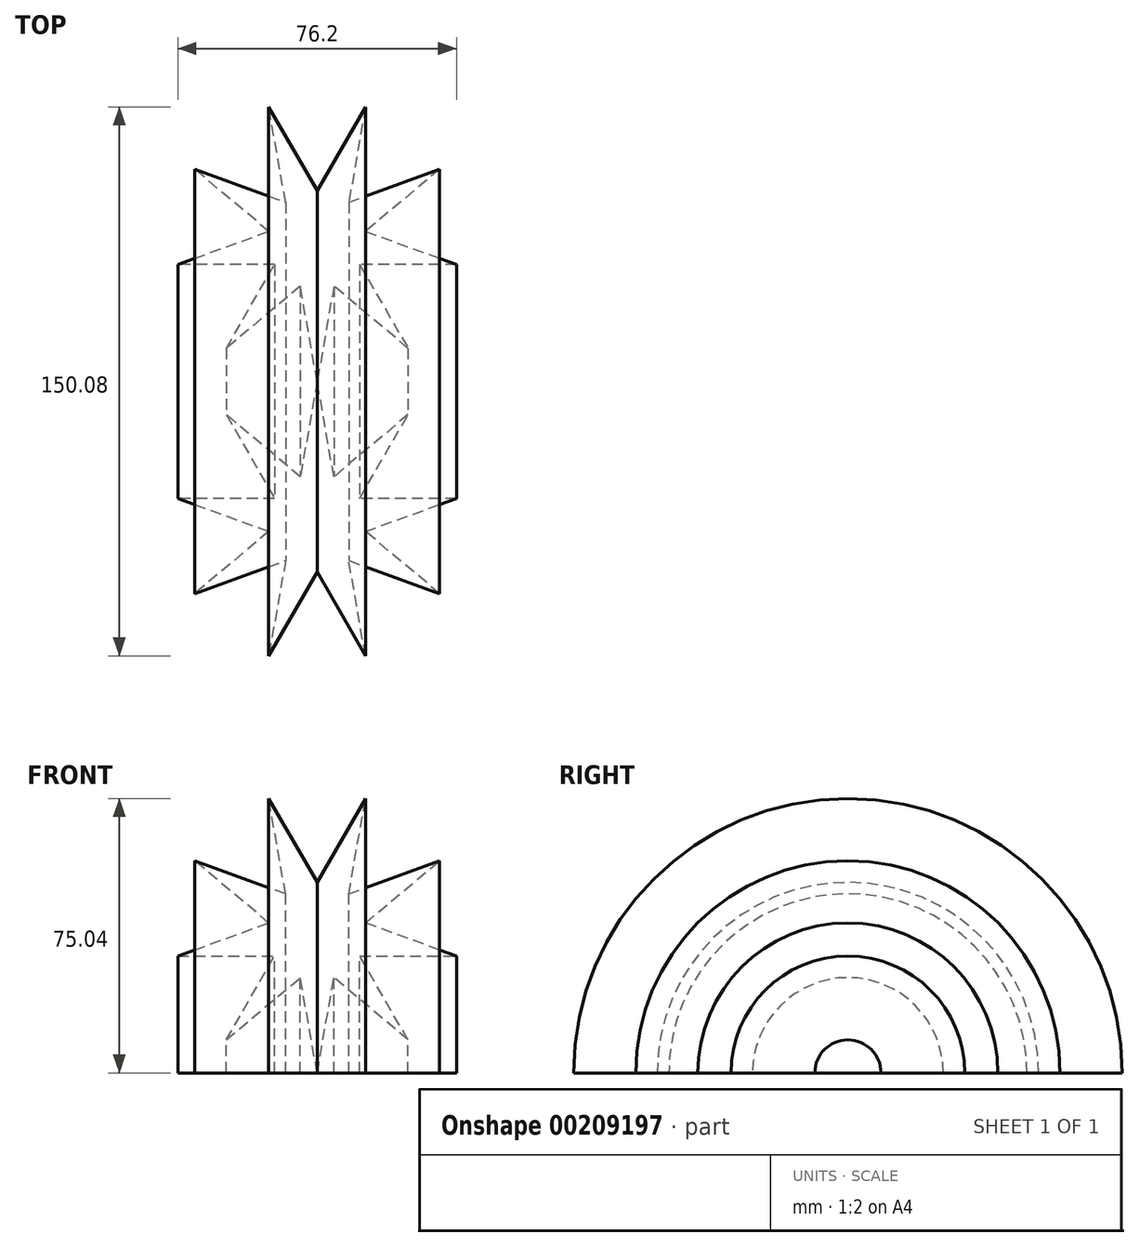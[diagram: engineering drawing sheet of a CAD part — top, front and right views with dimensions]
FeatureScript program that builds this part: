
annotation { "Feature Type Name" : "Feature", "Feature Type Description" : "" }
export const myFeature = defineFeature(function(context is Context, id is Id, definition is map)
    precondition{}
    {
        {
            var Q0;
            Q0=qCreatedBy(makeId("Top.planeOp"),FACE);
            var sketch = newSketch(context, id + "F0", { "sketchPlane" : qUnion([Q0])});
            skLineSegment(sketch, "E0", {"start": v(0, 0) * mm, "end": v(-13.23, -75.04) * mm});
            skLineSegment(sketch, "E1", {"start": v(-13.23, -75.04) * mm, "end": v(24.87, -9.05) * mm});
            skLineSegment(sketch, "E2", {"start": v(24.87, -9.05) * mm, "end": v(-33.5, -58.03) * mm});
            skLineSegment(sketch, "E3", {"start": v(-33.5, -58.03) * mm, "end": v(38.1, -31.97) * mm});
            skLineSegment(sketch, "E4", {"start": v(38.1, -31.97) * mm, "end": v(-38.1, -31.97) * mm});
            skLineSegment(sketch, "E5", {"start": v(-38.1, -31.97) * mm, "end": v(33.5, -58.03) * mm});
            skLineSegment(sketch, "E6", {"start": v(33.5, -58.03) * mm, "end": v(-24.87, -9.05) * mm});
            skLineSegment(sketch, "E7", {"start": v(-24.87, -9.05) * mm, "end": v(13.23, -75.04) * mm});
            skLineSegment(sketch, "E8", {"start": v(13.23, -75.04) * mm, "end": v(0, 0) * mm});
            skSolve(sketch);
        }
        {
            var Q0;
            Q0=qCreatedBy(makeId("Top.planeOp"),FACE);
            var sketch = newSketch(context, id + "F1", { "sketchPlane" : qUnion([Q0])});
            skLineSegment(sketch, "E9", {"start": v(31.65, 0) * mm, "end": v(-31.65, 0) * mm});
            skSolve(sketch);
        }
        {
            var Q0;
            {var subQ0=sQuery(id+"F0.wireOp",EDGE,"E8");var subQ1=sQuery(id+"F0.wireOp",EDGE,"E1");var subQ2=makeQuery(id+"F0.imprint","INTERSECT",VERTEX,{"derivedFrom":[subQ1,subQ0]});Q0=makeQuery(id+"F0.imprint","IMPRINT",FACE,{"disambiguationData":[TD([[makeQuery(id+"F0.imprint","IMPRINT",EDGE,{"disambiguationData":[TD([[subQ2,-1.0]])],"derivedFrom":subQ1}),1.0]])]});}
            var Q1;
            {var subQ0=sQuery(id+"F0.wireOp",EDGE,"E4");var subQ1=sQuery(id+"F0.wireOp",EDGE,"E1");var subQ2=makeQuery(id+"F0.imprint","INTERSECT",VERTEX,{"derivedFrom":[subQ1,subQ0]});Q1=makeQuery(id+"F0.imprint","IMPRINT",FACE,{"disambiguationData":[TD([[makeQuery(id+"F0.imprint","IMPRINT",EDGE,{"disambiguationData":[TD([[subQ2,1.0]])],"derivedFrom":subQ1}),-1.0]])]});}
            var Q2;
            {var subQ0=sQuery(id+"F0.wireOp",EDGE,"E3");var subQ1=sQuery(id+"F0.wireOp",EDGE,"E0");var subQ2=makeQuery(id+"F0.imprint","INTERSECT",VERTEX,{"derivedFrom":[subQ1,subQ0]});Q2=makeQuery(id+"F0.imprint","IMPRINT",FACE,{"disambiguationData":[TD([[makeQuery(id+"F0.imprint","IMPRINT",EDGE,{"disambiguationData":[TD([[subQ2,1.0]])],"derivedFrom":subQ1}),1.0]])]});}
            var Q3;
            {var subQ0=sQuery(id+"F0.wireOp",EDGE,"E8");var subQ1=sQuery(id+"F0.wireOp",EDGE,"E1");var subQ2=makeQuery(id+"F0.imprint","INTERSECT",VERTEX,{"derivedFrom":[subQ1,subQ0]});Q3=makeQuery(id+"F0.imprint","IMPRINT",FACE,{"disambiguationData":[TD([[makeQuery(id+"F0.imprint","IMPRINT",EDGE,{"disambiguationData":[TD([[subQ2,-1.0]])],"derivedFrom":subQ1}),-1.0]])]});}
            var Q4;
            {var subQ0=sQuery(id+"F0.wireOp",EDGE,"E3");var subQ1=sQuery(id+"F0.wireOp",EDGE,"E0");var subQ2=makeQuery(id+"F0.imprint","INTERSECT",VERTEX,{"derivedFrom":[subQ1,subQ0]});Q4=makeQuery(id+"F0.imprint","IMPRINT",FACE,{"disambiguationData":[TD([[makeQuery(id+"F0.imprint","IMPRINT",EDGE,{"disambiguationData":[TD([[subQ2,1.0]])],"derivedFrom":subQ1}),-1.0]])]});}
            var Q5;
            {var subQ0=sQuery(id+"F0.wireOp",EDGE,"E8");var subQ1=sQuery(id+"F0.wireOp",EDGE,"E2");var subQ2=makeQuery(id+"F0.imprint","INTERSECT",VERTEX,{"derivedFrom":[subQ1,subQ0]});Q5=makeQuery(id+"F0.imprint","IMPRINT",FACE,{"disambiguationData":[TD([[makeQuery(id+"F0.imprint","IMPRINT",EDGE,{"disambiguationData":[TD([[subQ2,-1.0]])],"derivedFrom":subQ1}),1.0]])]});}
            var Q6;
            {var subQ0=sQuery(id+"F0.wireOp",EDGE,"E5");var subQ1=sQuery(id+"F0.wireOp",EDGE,"E2");var subQ2=makeQuery(id+"F0.imprint","INTERSECT",VERTEX,{"derivedFrom":[subQ1,subQ0]});Q6=makeQuery(id+"F0.imprint","IMPRINT",FACE,{"disambiguationData":[TD([[makeQuery(id+"F0.imprint","IMPRINT",EDGE,{"disambiguationData":[TD([[subQ2,1.0]])],"derivedFrom":subQ1}),-1.0]])]});}
            var Q7;
            {var subQ0=sQuery(id+"F0.wireOp",EDGE,"E6");var subQ1=sQuery(id+"F0.wireOp",EDGE,"E3");var subQ2=makeQuery(id+"F0.imprint","INTERSECT",VERTEX,{"derivedFrom":[subQ1,subQ0]});Q7=makeQuery(id+"F0.imprint","IMPRINT",FACE,{"disambiguationData":[TD([[makeQuery(id+"F0.imprint","IMPRINT",EDGE,{"disambiguationData":[TD([[subQ2,1.0]])],"derivedFrom":subQ1}),-1.0]])]});}
            var Q8;
            {var subQ0=sQuery(id+"F0.wireOp",EDGE,"E7");var subQ1=sQuery(id+"F0.wireOp",EDGE,"E1");var subQ2=makeQuery(id+"F0.imprint","INTERSECT",VERTEX,{"derivedFrom":[subQ1,subQ0]});Q8=makeQuery(id+"F0.imprint","IMPRINT",FACE,{"disambiguationData":[TD([[makeQuery(id+"F0.imprint","IMPRINT",EDGE,{"disambiguationData":[TD([[subQ2,-1.0]])],"derivedFrom":subQ1}),1.0]])]});}
            var Q9;
            {var subQ0=sQuery(id+"F0.wireOp",EDGE,"E2");var subQ1=sQuery(id+"F0.wireOp",EDGE,"E0");var subQ2=makeQuery(id+"F0.imprint","INTERSECT",VERTEX,{"derivedFrom":[subQ1,subQ0]});Q9=makeQuery(id+"F0.imprint","IMPRINT",FACE,{"disambiguationData":[TD([[makeQuery(id+"F0.imprint","IMPRINT",EDGE,{"disambiguationData":[TD([[subQ2,-1.0]])],"derivedFrom":subQ1}),-1.0]])]});}
            var Q10;
            {var subQ5=sQuery(id+"F0.wireOp",EDGE,"E2");var subQ6=sQuery(id+"F0.wireOp",EDGE,"E0");var subQ7=makeQuery(id+"F0.imprint","INTERSECT",VERTEX,{"derivedFrom":[subQ6,subQ5]});Q10=makeQuery(id+"F0.imprint","IMPRINT",FACE,{"disambiguationData":[TD([[makeQuery(id+"F0.imprint","IMPRINT",EDGE,{"disambiguationData":[TD([[subQ7,-1.0]])],"derivedFrom":subQ6}),1.0]])]});}
            var Q11;
            {var subQ0=sQuery(id+"F0.wireOp",EDGE,"E5");var subQ1=sQuery(id+"F0.wireOp",EDGE,"E1");var subQ2=makeQuery(id+"F0.imprint","INTERSECT",VERTEX,{"derivedFrom":[subQ1,subQ0]});Q11=makeQuery(id+"F0.imprint","IMPRINT",FACE,{"disambiguationData":[TD([[makeQuery(id+"F0.imprint","IMPRINT",EDGE,{"disambiguationData":[TD([[subQ2,-1.0]])],"derivedFrom":subQ1}),-1.0]])]});}
            var Q12;
            {var subQ0=sQuery(id+"F0.wireOp",EDGE,"E6");var subQ1=sQuery(id+"F0.wireOp",EDGE,"E0");var subQ2=makeQuery(id+"F0.imprint","INTERSECT",VERTEX,{"derivedFrom":[subQ1,subQ0]});Q12=makeQuery(id+"F0.imprint","IMPRINT",FACE,{"disambiguationData":[TD([[makeQuery(id+"F0.imprint","IMPRINT",EDGE,{"disambiguationData":[TD([[subQ2,-1.0]])],"derivedFrom":subQ1}),-1.0]])]});}
            var Q13;
            {var subQ0=sQuery(id+"F0.wireOp",EDGE,"E1");var subQ1=sQuery(id+"F0.wireOp",EDGE,"E0");var subQ2=makeQuery(id+"F0.imprint","INTERSECT",VERTEX,{"derivedFrom":[subQ1,subQ0]});Q13=makeQuery(id+"F0.imprint","IMPRINT",FACE,{"disambiguationData":[TD([[makeQuery(id+"F0.imprint","IMPRINT",EDGE,{"disambiguationData":[TD([[subQ2,1.0]])],"derivedFrom":subQ1}),1.0]])]});}
            var Q14;
            {var subQ0=sQuery(id+"F0.wireOp",EDGE,"E4");var subQ1=sQuery(id+"F0.wireOp",EDGE,"E1");var subQ2=makeQuery(id+"F0.imprint","INTERSECT",VERTEX,{"derivedFrom":[subQ1,subQ0]});Q14=makeQuery(id+"F0.imprint","IMPRINT",FACE,{"disambiguationData":[TD([[makeQuery(id+"F0.imprint","IMPRINT",EDGE,{"disambiguationData":[TD([[subQ2,1.0]])],"derivedFrom":subQ1}),1.0]])]});}
            var Q15;
            {var subQ0=sQuery(id+"F0.wireOp",EDGE,"E7");var subQ1=sQuery(id+"F0.wireOp",EDGE,"E1");var subQ2=makeQuery(id+"F0.imprint","INTERSECT",VERTEX,{"derivedFrom":[subQ1,subQ0]});Q15=makeQuery(id+"F0.imprint","IMPRINT",FACE,{"disambiguationData":[TD([[makeQuery(id+"F0.imprint","IMPRINT",EDGE,{"disambiguationData":[TD([[subQ2,-1.0]])],"derivedFrom":subQ1}),-1.0]])]});}
            var Q16;
            {var subQ0=sQuery(id+"F0.wireOp",EDGE,"E2");var subQ1=sQuery(id+"F0.wireOp",EDGE,"E1");var subQ2=makeQuery(id+"F0.imprint","INTERSECT",VERTEX,{"derivedFrom":[subQ1,subQ0]});Q16=makeQuery(id+"F0.imprint","IMPRINT",FACE,{"disambiguationData":[TD([[makeQuery(id+"F0.imprint","IMPRINT",EDGE,{"disambiguationData":[TD([[subQ2,1.0]])],"derivedFrom":subQ1}),1.0]])]});}
            var Q17;
            {var subQ0=sQuery(id+"F0.wireOp",EDGE,"E7");var subQ1=sQuery(id+"F0.wireOp",EDGE,"E0");var subQ2=makeQuery(id+"F0.imprint","INTERSECT",VERTEX,{"derivedFrom":[subQ1,subQ0]});Q17=makeQuery(id+"F0.imprint","IMPRINT",FACE,{"disambiguationData":[TD([[makeQuery(id+"F0.imprint","IMPRINT",EDGE,{"disambiguationData":[TD([[subQ2,-1.0]])],"derivedFrom":subQ1}),-1.0]])]});}
            var Q18;
            {var subQ0=sQuery(id+"F0.wireOp",EDGE,"E6");var subQ1=sQuery(id+"F0.wireOp",EDGE,"E0");var subQ2=makeQuery(id+"F0.imprint","INTERSECT",VERTEX,{"derivedFrom":[subQ1,subQ0]});Q18=makeQuery(id+"F0.imprint","IMPRINT",FACE,{"disambiguationData":[TD([[makeQuery(id+"F0.imprint","IMPRINT",EDGE,{"disambiguationData":[TD([[subQ2,-1.0]])],"derivedFrom":subQ1}),1.0]])]});}
            var Q19;
            {var subQ0=sQuery(id+"F0.wireOp",EDGE,"E4");var subQ1=sQuery(id+"F0.wireOp",EDGE,"E0");var subQ2=makeQuery(id+"F0.imprint","INTERSECT",VERTEX,{"derivedFrom":[subQ1,subQ0]});Q19=makeQuery(id+"F0.imprint","IMPRINT",FACE,{"disambiguationData":[TD([[makeQuery(id+"F0.imprint","IMPRINT",EDGE,{"disambiguationData":[TD([[subQ2,-1.0]])],"derivedFrom":subQ1}),-1.0]])]});}
            var Q20;
            {var subQ0=sQuery(id+"F0.wireOp",EDGE,"E7");var subQ1=sQuery(id+"F0.wireOp",EDGE,"E3");var subQ2=makeQuery(id+"F0.imprint","INTERSECT",VERTEX,{"derivedFrom":[subQ1,subQ0]});Q20=makeQuery(id+"F0.imprint","IMPRINT",FACE,{"disambiguationData":[TD([[makeQuery(id+"F0.imprint","IMPRINT",EDGE,{"disambiguationData":[TD([[subQ2,-1.0]])],"derivedFrom":subQ1}),1.0]])]});}
            var Q21;
            {var subQ0=sQuery(id+"F0.wireOp",EDGE,"E6");var subQ1=sQuery(id+"F0.wireOp",EDGE,"E2");var subQ2=makeQuery(id+"F0.imprint","INTERSECT",VERTEX,{"derivedFrom":[subQ1,subQ0]});Q21=makeQuery(id+"F0.imprint","IMPRINT",FACE,{"disambiguationData":[TD([[makeQuery(id+"F0.imprint","IMPRINT",EDGE,{"disambiguationData":[TD([[subQ2,-1.0]])],"derivedFrom":subQ1}),1.0]])]});}
            var Q22;
            {var subQ0=sQuery(id+"F0.wireOp",EDGE,"E7");var subQ1=sQuery(id+"F0.wireOp",EDGE,"E0");var subQ2=makeQuery(id+"F0.imprint","INTERSECT",VERTEX,{"derivedFrom":[subQ1,subQ0]});Q22=makeQuery(id+"F0.imprint","IMPRINT",FACE,{"disambiguationData":[TD([[makeQuery(id+"F0.imprint","IMPRINT",EDGE,{"disambiguationData":[TD([[subQ2,-1.0]])],"derivedFrom":subQ1}),1.0]])]});}
            var Q23;
            {var subQ0=sQuery(id+"F0.wireOp",EDGE,"E5");var subQ1=sQuery(id+"F0.wireOp",EDGE,"E1");var subQ2=makeQuery(id+"F0.imprint","INTERSECT",VERTEX,{"derivedFrom":[subQ1,subQ0]});Q23=makeQuery(id+"F0.imprint","IMPRINT",FACE,{"disambiguationData":[TD([[makeQuery(id+"F0.imprint","IMPRINT",EDGE,{"disambiguationData":[TD([[subQ2,-1.0]])],"derivedFrom":subQ1}),1.0]])]});}
            var Q24;
            {var subQ0=sQuery(id+"F0.wireOp",EDGE,"E8");var subQ1=sQuery(id+"F0.wireOp",EDGE,"E4");var subQ2=makeQuery(id+"F0.imprint","INTERSECT",VERTEX,{"derivedFrom":[subQ1,subQ0]});Q24=makeQuery(id+"F0.imprint","IMPRINT",FACE,{"disambiguationData":[TD([[makeQuery(id+"F0.imprint","IMPRINT",EDGE,{"disambiguationData":[TD([[subQ2,-1.0]])],"derivedFrom":subQ1}),1.0]])]});}
            var Q25;
            {var subQ0=sQuery(id+"F0.wireOp",EDGE,"E4");var subQ1=sQuery(id+"F0.wireOp",EDGE,"E0");var subQ2=makeQuery(id+"F0.imprint","INTERSECT",VERTEX,{"derivedFrom":[subQ1,subQ0]});Q25=makeQuery(id+"F0.imprint","IMPRINT",FACE,{"disambiguationData":[TD([[makeQuery(id+"F0.imprint","IMPRINT",EDGE,{"disambiguationData":[TD([[subQ2,-1.0]])],"derivedFrom":subQ1}),1.0]])]});}
            var Q26;
            {var subQ0=sQuery(id+"F0.wireOp",EDGE,"E3");var subQ1=sQuery(id+"F0.wireOp",EDGE,"E1");var subQ2=makeQuery(id+"F0.imprint","INTERSECT",VERTEX,{"derivedFrom":[subQ1,subQ0]});Q26=makeQuery(id+"F0.imprint","IMPRINT",FACE,{"disambiguationData":[TD([[makeQuery(id+"F0.imprint","IMPRINT",EDGE,{"disambiguationData":[TD([[subQ2,-1.0]])],"derivedFrom":subQ1}),-1.0]])]});}
            var Q27;
            {var subQ0=sQuery(id+"F0.wireOp",EDGE,"E8");var subQ1=sQuery(id+"F0.wireOp",EDGE,"E0");var subQ2=makeQuery(id+"F0.imprint","INTERSECT",VERTEX,{"derivedFrom":[subQ1,subQ0]});Q27=makeQuery(id+"F0.imprint","IMPRINT",FACE,{"disambiguationData":[TD([[makeQuery(id+"F0.imprint","IMPRINT",EDGE,{"disambiguationData":[TD([[subQ2,-1.0]])],"derivedFrom":subQ1}),1.0]])]});}
            var Q28;
            Q28=sQuery(id+"F1.wireOp",EDGE,"E9");
            revolve(context, id + "F2", {"entities" : qUnion([Q0, Q1, Q2, Q3, Q4, Q5, Q6, Q7, Q8, Q9, Q10, Q11, Q12, Q13, Q14, Q15, Q16, Q17, Q18, Q19, Q20, Q21, Q22, Q23, Q24, Q25, Q26, Q27]), "axis" : qUnion([Q28]), "revolveType" : RevolveType.ONE_DIRECTION, "angle" : 180 * degree});
        }
    });
